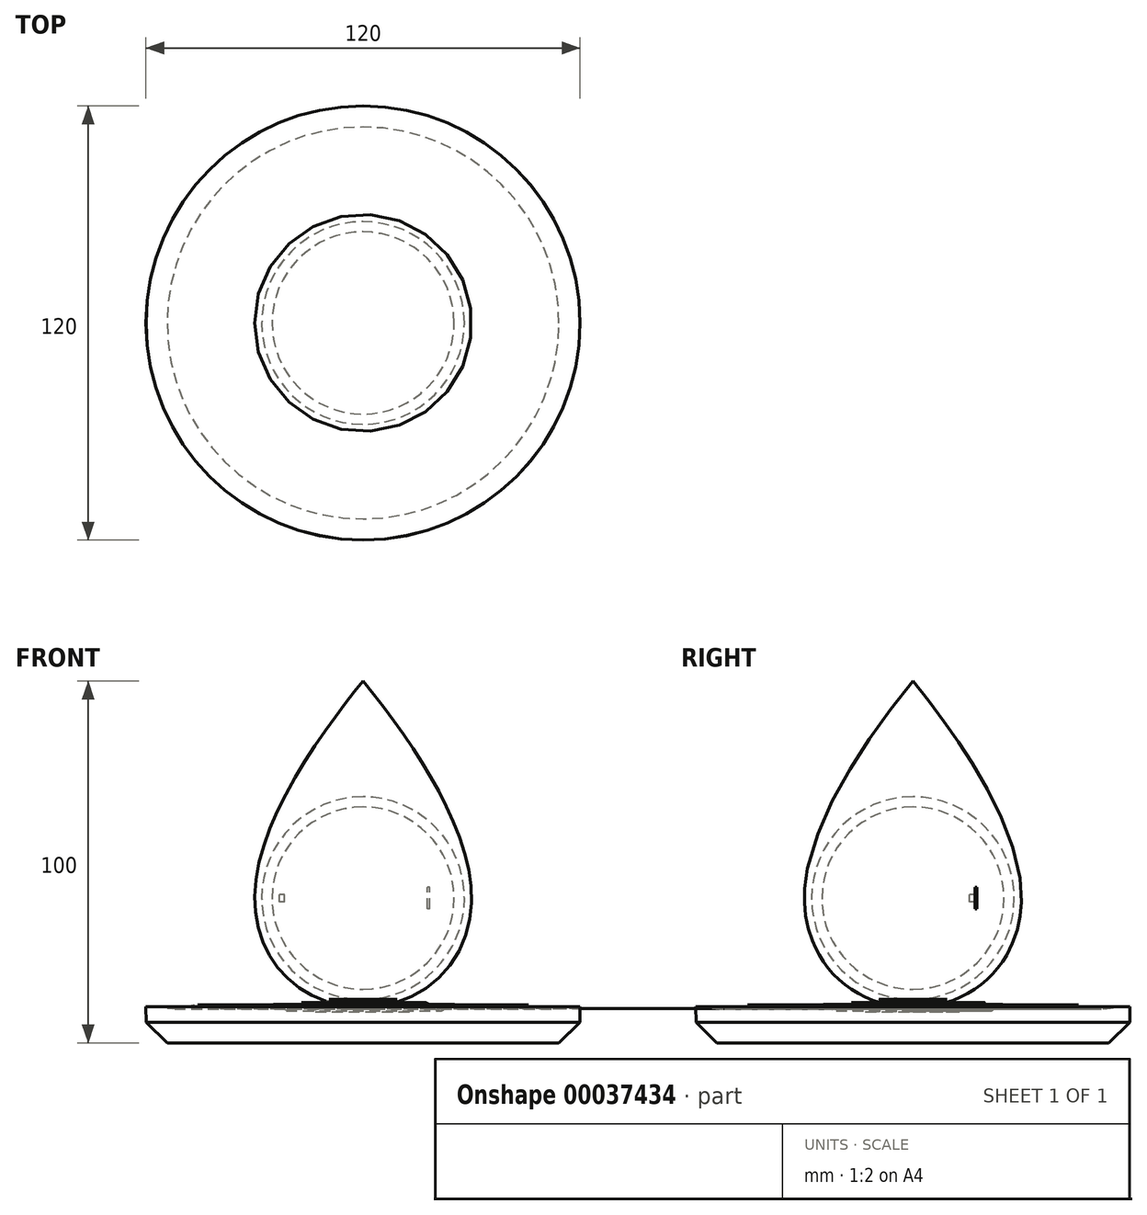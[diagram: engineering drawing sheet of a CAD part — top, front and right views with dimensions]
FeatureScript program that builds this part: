
annotation { "Feature Type Name" : "Feature", "Feature Type Description" : "" }
export const myFeature = defineFeature(function(context is Context, id is Id, definition is map)
    precondition{}
    {
        {
            var Q0;
            Q0=qCreatedBy(makeId("Front.planeOp"),FACE);
            var sketch = newSketch(context, id + "F0", { "sketchPlane" : qUnion([Q0])});
            skLineSegment(sketch, "E0", {"start": v(0, 0) * mm, "end": v(0, 60) * mm, "construction": true});
            skCircle(sketch, "E1", {"center": v(0, 0) * mm, "radius": 30 * mm, "construction": true});
            skFitSpline(sketch, "E2", {"points": [v(-30, 0) * mm, v(0, 60) * mm], "startDerivative": vector(0, 60.9) * mm, "endDerivative": vector(31.62, 38.72) * mm});
            skArc(sketch, "E3", {"start": v(-30, 0) * mm, "mid": v(-21.21, -21.21) * mm, "end": v(0, -30) * mm});
            skLineSegment(sketch, "E4", {"start": v(0, -30) * mm, "end": v(-60, -30) * mm, "construction": true});
            skFitSpline(sketch, "E5", {"points": [v(0, -30) * mm, v(-14.56, -28.66) * mm, v(-17.87, -32.8) * mm, v(-25.55, -26.14) * mm, v(-34.76, -32) * mm, v(-41.27, -28.61) * mm, v(-60, -30) * mm], "startDerivative": vector(-150.62, 0) * mm, "endDerivative": vector(-191.12, -2.3) * mm});
            skLineSegment(sketch, "E6", {"start": v(0, -30) * mm, "end": v(59.77, -35.23) * mm, "construction": true});
            skFitSpline(sketch, "E7.MirrorCS", {"points": [v(0, -30) * mm, v(13.01, -28.56) * mm, v(17.15, -33.74) * mm, v(27.4, -28.46) * mm, v(36.71, -35.07) * mm, v(45.9, -32.1) * mm, v(63.2, -35.36) * mm], "startDerivative": vector(150.65, 0) * mm, "endDerivative": vector(191.13, -2) * mm, "construction": true});
            skFitSpline(sketch, "E8", {"points": [v(59.77, -35.23) * mm, v(22.24, -44.88) * mm], "startDerivative": vector(-82.92, -3.86) * mm, "endDerivative": vector(-5.17, -14.08) * mm, "construction": true});
            skLineSegment(sketch, "E9", {"start": v(-54.15, -40) * mm, "end": v(0, -40) * mm});
            skFitSpline(sketch, "E10", {"points": [v(0, 60) * mm, v(-30, 0) * mm, v(0, -30) * mm], "startDerivative": vector(-56.77, -69.51) * mm, "endDerivative": vector(119.82, 2.18) * mm});
            skLineSegment(sketch, "E11", {"start": v(-60, -30) * mm, "end": v(-59.95, -34.38) * mm});
            skLineSegment(sketch, "E12", {"start": v(-59.95, -34.38) * mm, "end": v(-54.15, -40) * mm});
            skSolve(sketch);
        }
        {
            var Q0;
            Q0=qCreatedBy(makeId("Front.planeOp"),FACE);
            var sketch = newSketch(context, id + "F1", { "sketchPlane" : qUnion([Q0])});
            skLineSegment(sketch, "E13", {"start": v(0, 0) * mm, "end": v(0, -30) * mm, "construction": true});
            skLineSegment(sketch, "E14", {"start": v(0, -30) * mm, "end": v(-60, -30) * mm, "construction": true});
            skFitSpline(sketch, "E15", {"points": [v(0, -30) * mm, v(-6.93, -30) * mm, v(-9.66, -28) * mm, v(-13.1, -31.46) * mm, v(-16.8, -28.87) * mm, v(-21.1, -31.2) * mm, v(-24.41, -29.44) * mm, v(-28.76, -30.61) * mm, v(-33.98, -29.54) * mm, v(-39.2, -30.56) * mm, v(-45.65, -29.49) * mm, v(-51.27, -30.66) * mm, v(-60, -30) * mm], "startDerivative": vector(-82.62, -16.89) * mm, "endDerivative": vector(-120.42, 0) * mm});
            skSolve(sketch);
        }
        {
            var Q0;
            Q0 = qSketchRegion(id + "F0", true);
            var Q1;
            Q1=sQuery(id+"F0.wireOp",EDGE,"5a3c826f-a51e-4b3e-ae52-6c5c029438bf");
            var Q2;
            Q2=sQuery(id+"F0.wireOp",EDGE,"E9");
            var Q3;
            Q3=sQuery(id+"F0.wireOp",EDGE,"E10");
            var Q4;
            Q4=sQuery(id+"F0.wireOp",EDGE,"E11");
            var Q5;
            Q5=sQuery(id+"F0.wireOp",EDGE,"E12");
            var Q6;
            Q6=sQuery(id+"F0.wireOp",EDGE,"E0");
            revolve(context, id + "F2", {"bodyType" : ToolBodyType.SURFACE, "entities" : qUnion([Q0]), "surfaceEntities" : qUnion([Q1, Q2, Q3, Q4, Q5]), "axis" : qUnion([Q6]), "revolveType" : RevolveType.FULL});
        }
        {
            var Q0;
            Q0 = qSketchRegion(id + "F1", true);
            var Q1;
            Q1=sQuery(id+"F1.wireOp",EDGE,"E15");
            var Q2;
            Q2=sQuery(id+"F1.wireOp",EDGE,"E13");
            revolve(context, id + "F3", {"bodyType" : ToolBodyType.SURFACE, "entities" : qUnion([Q0]), "surfaceEntities" : qUnion([Q1]), "axis" : qUnion([Q2]), "revolveType" : RevolveType.FULL});
        }
        {
            var Q0;
            Q0=qCreatedBy(makeId("Front.planeOp"),FACE);
            var sketch = newSketch(context, id + "F4", { "sketchPlane" : qUnion([Q0])});
            skArc(sketch, "E16", {"start": v(0, 28.01) * mm, "mid": v(-28.01, 0) * mm, "end": v(0, -28.01) * mm});
            skArc(sketch, "E17", {"start": v(0, 25.18) * mm, "mid": v(-25.18, 0) * mm, "end": v(0, -25.18) * mm});
            skLineSegment(sketch, "E18", {"start": v(0, 28.01) * mm, "end": v(0, -28.01) * mm, "construction": true});
            skSolve(sketch);
        }
        {
            var Q0;
            Q0=sQuery(id+"F4.wireOp",EDGE,"E18");
            var Q1;
            Q1=sQuery(id+"F4.wireOp",EDGE,"E16");
            var Q2;
            Q2=sQuery(id+"F4.wireOp",EDGE,"E17");
            var Q3;
            Q3=sQuery(id+"F4.wireOp",EDGE,"E18");
            revolve(context, id + "F5", {"bodyType" : ToolBodyType.SURFACE, "surfaceEntities" : qUnion([Q0, Q1, Q2]), "axis" : qUnion([Q3]), "revolveType" : RevolveType.FULL});
        }
        {
            var Q0;
            Q0=qCreatedBy(makeId("Top.planeOp"),FACE);
            var sketch = newSketch(context, id + "F6", { "sketchPlane" : qUnion([Q0])});
            skArc(sketch, "E19", {"start": v(-21.77, 17.5) * mm, "mid": v(-22.47, 16.58) * mm, "end": v(-23.14, 15.64) * mm});
            skArc(sketch, "E20", {"start": v(18.37, 17.17) * mm, "mid": v(18.1, 17.45) * mm, "end": v(17.82, 17.74) * mm});
            skSolve(sketch);
        }
        {
            var Q0;
            Q0=sQuery(id+"F6.wireOp",EDGE,"E19");
            extrude(context, id + "F7", {"bodyType" : ToolBodyType.SURFACE, "surfaceEntities" : qUnion([Q0]), "endBound" : BoundingType.SYMMETRIC, "depth" : 2 * mm});
        }
        {
            var Q0;
            Q0 = qSketchRegion(id + "F6", true);
            var Q1;
            Q1=sQuery(id+"F6.wireOp",EDGE,"E20");
            extrude(context, id + "F8", {"entities" : qUnion([Q0]), "bodyType" : ToolBodyType.SURFACE, "surfaceEntities" : qUnion([Q1]), "endBound" : BoundingType.SYMMETRIC, "depth" : 6 * mm});
        }
    });
